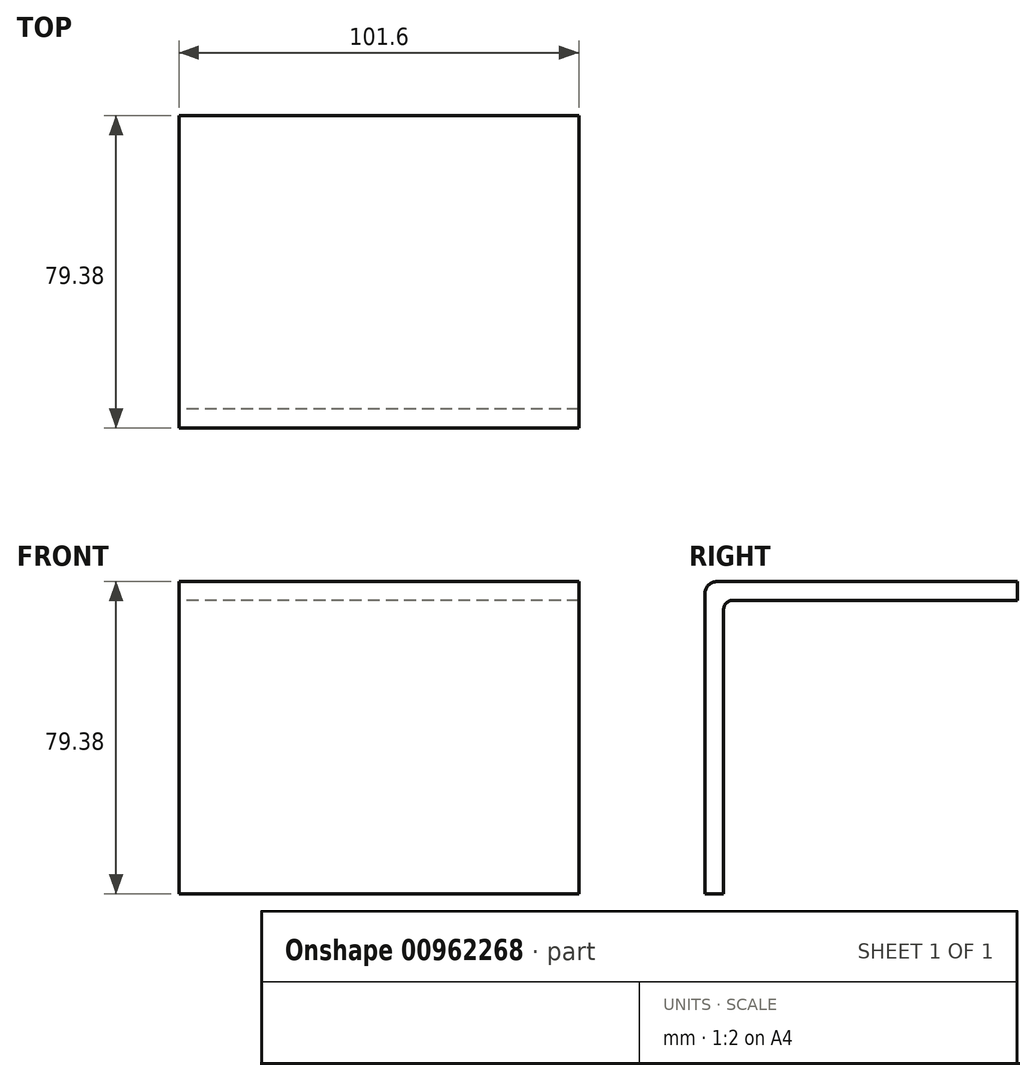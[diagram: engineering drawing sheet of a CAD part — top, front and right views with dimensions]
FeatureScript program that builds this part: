
annotation { "Feature Type Name" : "Feature", "Feature Type Description" : "" }
export const myFeature = defineFeature(function(context is Context, id is Id, definition is map)
    precondition{}
    {
        {
            var Q0;
            Q0=qCreatedBy(makeId("Right.planeOp"),FACE);
            var sketch = newSketch(context, id + "F0", { "sketchPlane" : qUnion([Q0])});
            skLineSegment(sketch, "E0", {"start": v(0, 0) * mm, "end": v(79.38, 0) * mm});
            skLineSegment(sketch, "E1", {"start": v(79.38, 0) * mm, "end": v(79.38, -4.76) * mm});
            skLineSegment(sketch, "E2", {"start": v(79.38, -4.76) * mm, "end": v(4.76, -4.76) * mm});
            skLineSegment(sketch, "E3", {"start": v(4.76, -4.76) * mm, "end": v(4.76, -79.38) * mm});
            skLineSegment(sketch, "E4", {"start": v(4.76, -79.38) * mm, "end": v(0, -79.38) * mm});
            skLineSegment(sketch, "E5", {"start": v(0, -79.38) * mm, "end": v(0, 0) * mm});
            skSolve(sketch);
        }
        {
            var Q0;
            Q0 = qSketchRegion(id + "F0", true);
            extrude(context, id + "F1", {"entities" : qUnion([Q0]), "depth" : 101.6 * mm, "offsetDistance" : 25.4 * mm});
        }
        {
            var Q0;
            Q0=makeQuery(id+"F1.opExtrude","SWEPT_EDGE",EDGE,{"disambiguationData":[OSD([sQuery(id+"F0.wireOp",EDGE,"E0"),sQuery(id+"F0.wireOp",EDGE,"E5")])]});
            fillet(context, id + "F2", {"entities" : qUnion([Q0]), "radius" : 3.17 * mm, "tangentPropagation" : true, "allowEdgeOverflow" : false});
        }
        {
            var Q0;
            Q0=makeQuery(id+"F1.opExtrude","SWEPT_EDGE",EDGE,{"disambiguationData":[OSD([sQuery(id+"F0.wireOp",EDGE,"E2"),sQuery(id+"F0.wireOp",EDGE,"E3")])]});
            fillet(context, id + "F3", {"entities" : qUnion([Q0]), "radius" : 2.41 * mm, "tangentPropagation" : true, "allowEdgeOverflow" : false});
        }
    });
